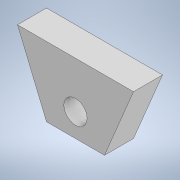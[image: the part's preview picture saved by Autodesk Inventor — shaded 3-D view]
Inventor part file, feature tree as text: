
AUTODESK INVENTOR PART (.ipt)
format: ipt  version: 2022 (Build 260153000, 153)  size: 96,768 bytes
history: native  units: mm
features: other x1, extrude x1, sketch x1
ambient origin geometry x8: Origin, YZ Plane, XZ Plane, XY Plane, X Axis, Y Axis, Z Axis, Center Point
bodies: Body1 (feature_tree)
feature tree (3):
  other  "Твердое тело1"
  extrude  "Выдавливание1"  Depth=24.0mm
  sketch  "Эскиз1"
